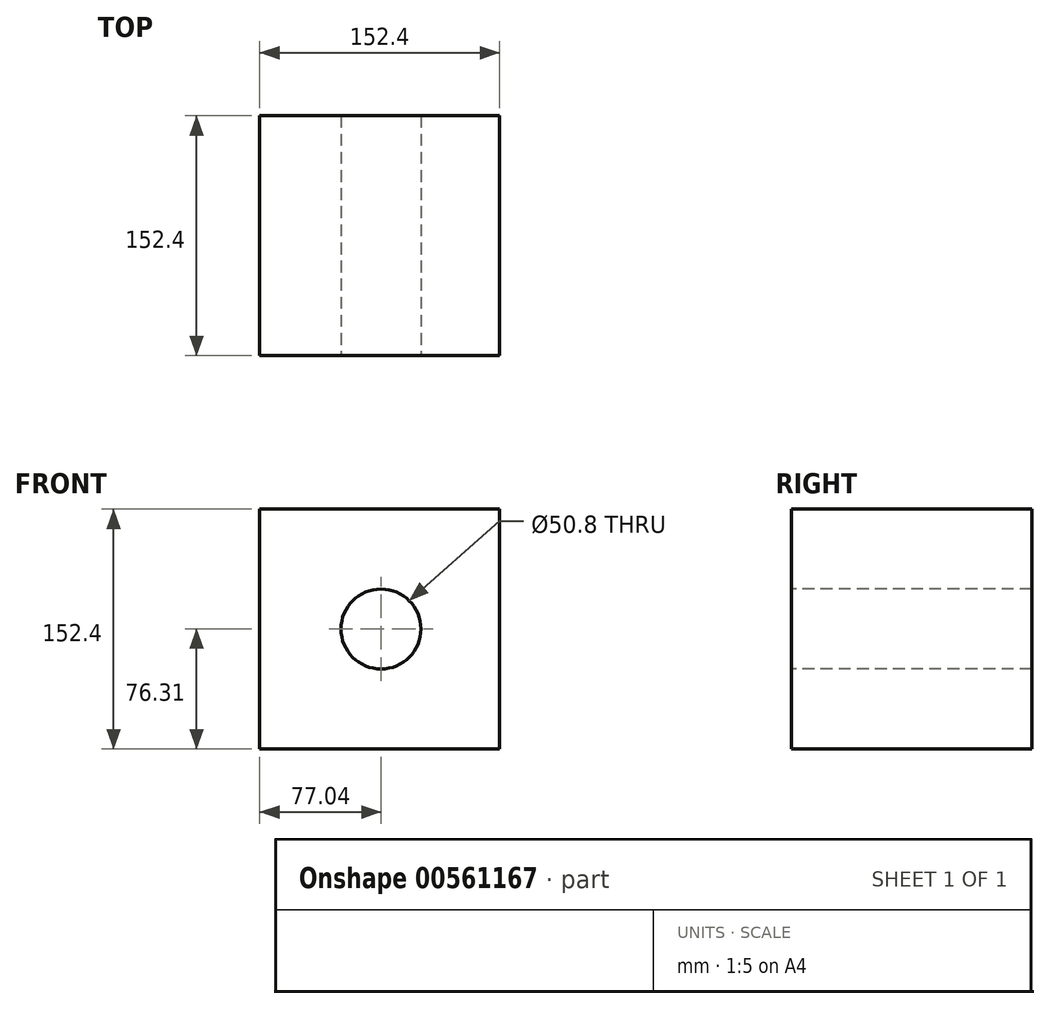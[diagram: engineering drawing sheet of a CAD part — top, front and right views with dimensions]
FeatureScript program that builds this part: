
annotation { "Feature Type Name" : "Feature", "Feature Type Description" : "" }
export const myFeature = defineFeature(function(context is Context, id is Id, definition is map)
    precondition{}
    {
        {
            var Q0;
            Q0=qCreatedBy(makeId("Front.planeOp"),FACE);
            var sketch = newSketch(context, id + "F0", { "sketchPlane" : qUnion([Q0])});
            skLineSegment(sketch, "E0.bottom", {"start": v(-77.04, 76.1) * mm, "end": v(75.36, 76.1) * mm});
            skLineSegment(sketch, "E0.top", {"start": v(-77.04, -76.3) * mm, "end": v(75.36, -76.3) * mm});
            skLineSegment(sketch, "E0.left", {"start": v(-77.04, 76.1) * mm, "end": v(-77.04, -76.3) * mm});
            skLineSegment(sketch, "E0.right", {"start": v(75.36, 76.1) * mm, "end": v(75.36, -76.3) * mm});
            skLineSegment(sketch, "E1.bottom", {"start": v(242.12, -141.52) * mm, "end": v(213.23, -141.52) * mm});
            skLineSegment(sketch, "E1.top", {"start": v(242.12, -139.21) * mm, "end": v(213.23, -139.21) * mm});
            skLineSegment(sketch, "E1.left", {"start": v(242.12, -141.52) * mm, "end": v(242.12, -139.21) * mm});
            skLineSegment(sketch, "E1.right", {"start": v(213.23, -141.52) * mm, "end": v(213.23, -139.21) * mm});
            skSolve(sketch);
        }
        {
            var Q0;
            Q0=makeQuery(id+"F0.imprint","IMPRINT",FACE,{"disambiguationData":[TD([[makeQuery(id+"F0.imprint","IMPRINT",EDGE,{"derivedFrom":sQuery(id+"F0.wireOp",EDGE,"E0.bottom")}),-1.0]])]});
            extrude(context, id + "F1", {"entities" : qUnion([Q0]), "depth" : 152.4 * mm, "offsetDistance" : 25.4 * mm});
        }
        {
            var Q0;
            Q0=makeQuery(id+"F1.opExtrude","CAP_FACE",FACE,{"disambiguationData":[OSD([sQuery(id+"F0.wireOp",EDGE,"E0.bottom"),sQuery(id+"F0.wireOp",EDGE,"E0.top"),sQuery(id+"F0.wireOp",EDGE,"E0.left"),sQuery(id+"F0.wireOp",EDGE,"E0.right")])],"isStart":false});
            var sketch = newSketch(context, id + "F2", { "sketchPlane" : qUnion([Q0])});
            skCircle(sketch, "E2", {"center": v(0, 0) * mm, "radius": 25.4 * mm});
            skSolve(sketch);
        }
        {
            var Q0;
            Q0 = qSketchRegion(id + "F2", true);
            extrude(context, id + "F3", {"entities" : qUnion([Q0]), "operationType" : NewBodyOperationType.REMOVE, "oppositeDirection" : true, "depth" : 152.4 * mm, "offsetDistance" : 25.4 * mm});
        }
    });
